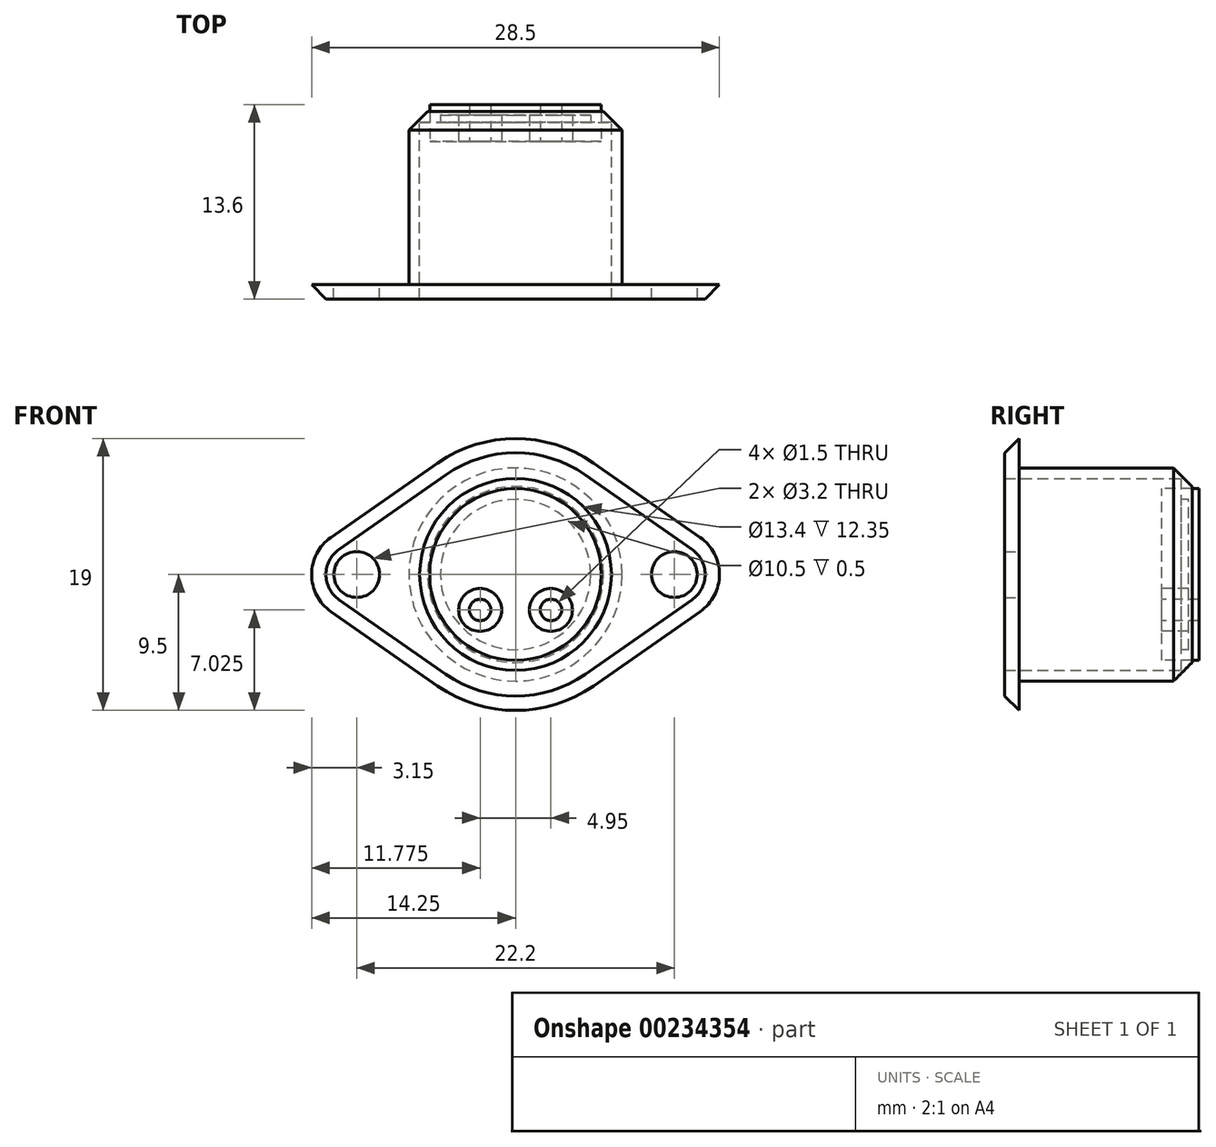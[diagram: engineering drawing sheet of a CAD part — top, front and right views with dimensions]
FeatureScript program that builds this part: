
annotation { "Feature Type Name" : "Feature", "Feature Type Description" : "" }
export const myFeature = defineFeature(function(context is Context, id is Id, definition is map)
    precondition{}
    {
        {
            var Q0;
            Q0=qCreatedBy(makeId("Front.planeOp"),FACE);
            var sketch = newSketch(context, id + "F0", { "sketchPlane" : qUnion([Q0])});
            skCircle(sketch, "E0", {"center": v(-11.1, 0) * mm, "radius": 1.6 * mm});
            skCircle(sketch, "E1", {"center": v(11.1, 0) * mm, "radius": 1.6 * mm});
            skArc(sketch, "E2", {"start": v(-12.9, 2.58) * mm, "mid": v(-14.25, 0) * mm, "end": v(-12.9, -2.58) * mm});
            skLineSegment(sketch, "E3", {"start": v(-14.25, 0) * mm, "end": v(14.25, 0) * mm, "construction": true});
            skCircle(sketch, "E4", {"center": v(0, 0) * mm, "radius": 6 * mm});
            skCircle(sketch, "E5", {"center": v(0, 0) * mm, "radius": 6.7 * mm});
            skArc(sketch, "E6", {"start": v(5.43, 7.8) * mm, "mid": v(0, 9.5) * mm, "end": v(-5.43, 7.8) * mm});
            skLineSegment(sketch, "E7", {"start": v(-12.9, 2.58) * mm, "end": v(-5.43, 7.8) * mm});
            skLineSegment(sketch, "E8", {"start": v(-12.9, -2.58) * mm, "end": v(-5.43, -7.8) * mm});
            skArc(sketch, "E9", {"start": v(12.9, -2.58) * mm, "mid": v(14.25, 0) * mm, "end": v(12.9, 2.58) * mm});
            skLineSegment(sketch, "E10", {"start": v(5.43, 7.8) * mm, "end": v(12.9, 2.58) * mm});
            skLineSegment(sketch, "E11", {"start": v(5.43, -7.8) * mm, "end": v(12.9, -2.58) * mm});
            skArc(sketch, "E12.trimOffspring", {"start": v(-5.43, -7.8) * mm, "mid": v(0, -9.5) * mm, "end": v(5.43, -7.8) * mm});
            skCircle(sketch, "E13.1.0", {"center": v(-2.47, 2.47) * mm, "radius": 0.75 * mm});
            skCircle(sketch, "E13.3.0", {"center": v(2.47, 2.47) * mm, "radius": 0.75 * mm});
            skLineSegment(sketch, "E13.anchor1", {"start": v(0, 0) * mm, "end": v(-3.5, 0) * mm, "construction": true});
            skLineSegment(sketch, "E13.anchor2", {"start": v(0, 0) * mm, "end": v(3.5, 0) * mm, "construction": true});
            skCircle(sketch, "E14", {"center": v(0, 0) * mm, "radius": 7.45 * mm});
            skLineSegment(sketch, "E15", {"start": v(0, 0) * mm, "end": v(2.47, 2.47) * mm, "construction": true});
            skLineSegment(sketch, "E16", {"start": v(0, 0) * mm, "end": v(-2.47, 2.47) * mm, "construction": true});
            skLineSegment(sketch, "E17.MirrorCS", {"start": v(0, 0) * mm, "end": v(-2.47, -2.47) * mm, "construction": true});
            skCircle(sketch, "E18.MirrorC", {"center": v(-2.47, -2.47) * mm, "radius": 0.75 * mm});
            skCircle(sketch, "E19.MirrorC", {"center": v(2.47, -2.47) * mm, "radius": 0.75 * mm});
            skLineSegment(sketch, "E20.left", {"start": v(-3.92, -1) * mm, "end": v(-3.92, 1) * mm});
            skLineSegment(sketch, "E21", {"start": v(0, -2.47) * mm, "end": v(0, 2.47) * mm, "construction": true});
            skLineSegment(sketch, "E22.MirrorCS", {"start": v(3.92, -1) * mm, "end": v(3.92, 1) * mm});
            skLineSegment(sketch, "E23", {"start": v(-3.92, 1) * mm, "end": v(-5.92, 1) * mm});
            skLineSegment(sketch, "E24", {"start": v(-3.92, -1) * mm, "end": v(-5.92, -1) * mm});
            skLineSegment(sketch, "E25.MirrorCS", {"start": v(3.92, 1) * mm, "end": v(5.92, 1) * mm});
            skLineSegment(sketch, "E26.MirrorCS", {"start": v(3.92, -1) * mm, "end": v(5.92, -1) * mm});
            skCircle(sketch, "E27", {"center": v(0, 0) * mm, "radius": 0.75 * mm});
            skSolve(sketch);
        }
        {
            var Q0;
            Q0=makeQuery(id+"F0.imprint","IMPRINT",FACE,{"disambiguationData":[TD([[makeQuery(id+"F0.imprint","IMPRINT",EDGE,{"derivedFrom":sQuery(id+"F0.wireOp",EDGE,"E0")}),-1.0]])]});
            var Q1;
            Q1=makeQuery(id+"F0.imprint","IMPRINT",FACE,{"disambiguationData":[TD([[makeQuery(id+"F0.imprint","IMPRINT",EDGE,{"derivedFrom":sQuery(id+"F0.wireOp",EDGE,"E5")}),-1.0]])]});
            extrude(context, id + "F1", {"entities" : qUnion([Q0, Q1]), "depth" : 1 * mm});
        }
        {
            var Q0;
            Q0=makeQuery(id+"F1.opExtrude","CAP_EDGE",EDGE,{"disambiguationData":[OSD([sQuery(id+"F0.wireOp",EDGE,"E7")])],"isStart":false});
            chamfer(context, id + "F2", {"entities" : qUnion([Q0]), "width" : 1 * mm, "tangentPropagation" : true});
        }
        {
            var Q0;
            Q0=makeQuery(id+"F0.imprint","IMPRINT",FACE,{"disambiguationData":[TD([[makeQuery(id+"F0.imprint","IMPRINT",EDGE,{"derivedFrom":sQuery(id+"F0.wireOp",EDGE,"E5")}),-1.0]])]});
            var Q1;
            Q1=makeQuery(id+"F0.imprint","IMPRINT",FACE,{"disambiguationData":[TD([[makeQuery(id+"F0.imprint","IMPRINT",EDGE,{"derivedFrom":sQuery(id+"F0.wireOp",EDGE,"E4")}),-1.0]])]});
            var Q2;
            Q2=makeQuery(id+"F0.imprint","IMPRINT",FACE,{"disambiguationData":[TD([[makeQuery(id+"F0.imprint","IMPRINT",EDGE,{"derivedFrom":sQuery(id+"F0.wireOp",EDGE,"E4")}),1.0]])]});
            var Q3;
            Q3=makeQuery(id+"F0.imprint","IMPRINT",FACE,{"disambiguationData":[TD([[makeQuery(id+"F0.imprint","IMPRINT",EDGE,{"derivedFrom":sQuery(id+"F0.wireOp",EDGE,"E18.MirrorC")}),-1.0]])]});
            var Q4;
            Q4=makeQuery(id+"F0.imprint","IMPRINT",FACE,{"disambiguationData":[TD([[makeQuery(id+"F0.imprint","IMPRINT",EDGE,{"derivedFrom":sQuery(id+"F0.wireOp",EDGE,"E19.MirrorC")}),-1.0]])]});
            var Q5;
            Q5=makeQuery(id+"F0.imprint","IMPRINT",FACE,{"disambiguationData":[TD([[makeQuery(id+"F0.imprint","IMPRINT",EDGE,{"derivedFrom":sQuery(id+"F0.wireOp",EDGE,"E13.1.0")}),1.0]])]});
            var Q6;
            Q6=makeQuery(id+"F0.imprint","IMPRINT",FACE,{"disambiguationData":[TD([[makeQuery(id+"F0.imprint","IMPRINT",EDGE,{"derivedFrom":sQuery(id+"F0.wireOp",EDGE,"E13.3.0")}),1.0]])]});
            var Q7;
            Q7=makeQuery(id+"F0.imprint","IMPRINT",FACE,{"disambiguationData":[TD([[makeQuery(id+"F0.imprint","IMPRINT",EDGE,{"derivedFrom":sQuery(id+"F0.wireOp",EDGE,"E20.left")}),1.0]])]});
            var Q8;
            Q8=makeQuery(id+"F0.imprint","IMPRINT",FACE,{"disambiguationData":[TD([[makeQuery(id+"F0.imprint","IMPRINT",EDGE,{"derivedFrom":sQuery(id+"F0.wireOp",EDGE,"E22.MirrorCS")}),-1.0]])]});
            var Q9;
            Q9=makeQuery(id+"F0.imprint","IMPRINT",FACE,{"disambiguationData":[TD([[makeQuery(id+"F0.imprint","IMPRINT",EDGE,{"derivedFrom":sQuery(id+"F0.wireOp",EDGE,"E27")}),1.0]])]});
            var Q10;
            Q10=sQuery(id+"F0.wireOp",EDGE,"E5");
            extrude(context, id + "F3", {"entities" : qUnion([Q0, Q1, Q2, Q3, Q4, Q5, Q6, Q7, Q8, Q9]), "operationType" : NewBodyOperationType.ADD, "surfaceEntities" : qUnion([Q10]), "oppositeDirection" : true, "depth" : 12.1 * mm});
        }
        {
            var Q0;
            Q0=makeQuery(id+"F3.opExtrude","CAP_FACE",FACE,{"disambiguationData":[OSD([sQuery(id+"F0.wireOp",EDGE,"E14")])],"isStart":true});
            shell(context, id + "F4", {"entities" : qUnion([Q0]), "thickness" : .75 * mm});
        }
        {
            var Q0;
            Q0=makeQuery(id+"F0.imprint","IMPRINT",FACE,{"disambiguationData":[TD([[makeQuery(id+"F0.imprint","IMPRINT",EDGE,{"derivedFrom":sQuery(id+"F0.wireOp",EDGE,"TtFvNPpV-GBaN-JR9W-IqtY-BeMt7pxMo1nd")}),-1.0]])]});
            var Q1;
            Q1=makeQuery(id+"F0.imprint","IMPRINT",FACE,{"disambiguationData":[TD([[makeQuery(id+"F0.imprint","IMPRINT",EDGE,{"derivedFrom":sQuery(id+"F0.wireOp",EDGE,"TtFvNPpV-GBaN-JR9W-IqtY-BeMt7pxMo1nd")}),1.0]])]});
            var Q2;
            Q2=makeQuery(id+"F0.imprint","IMPRINT",FACE,{"disambiguationData":[TD([[makeQuery(id+"F0.imprint","IMPRINT",EDGE,{"derivedFrom":sQuery(id+"F0.wireOp",EDGE,"E13.1.0")}),1.0]])]});
            var Q3;
            Q3=makeQuery(id+"F0.imprint","IMPRINT",FACE,{"disambiguationData":[TD([[makeQuery(id+"F0.imprint","IMPRINT",EDGE,{"derivedFrom":sQuery(id+"F0.wireOp",EDGE,"E13.2.0")}),1.0]])]});
            var Q4;
            Q4=makeQuery(id+"F0.imprint","IMPRINT",FACE,{"disambiguationData":[TD([[makeQuery(id+"F0.imprint","IMPRINT",EDGE,{"derivedFrom":sQuery(id+"F0.wireOp",EDGE,"E13.3.0")}),1.0]])]});
            var Q5;
            Q5=makeQuery(id+"F0.imprint","IMPRINT",FACE,{"disambiguationData":[TD([[makeQuery(id+"F0.imprint","IMPRINT",EDGE,{"derivedFrom":sQuery(id+"F0.wireOp",EDGE,"E13.4.0")}),1.0]])]});
            var Q6;
            {var subQ0=sQuery(id+"F0.wireOp",EDGE,"y8nhEUVQ-kyqU-Q8um-lzXM-BuWz2Y8k01lN");Q6=makeQuery(id+"F0.imprint","IMPRINT",FACE,{"disambiguationData":[TD([[makeQuery(id+"F0.imprint","IMPRINT",EDGE,{"derivedFrom":subQ0}),-1.0]])]});}
            var Q7;
            Q7=makeQuery(id+"F0.imprint","IMPRINT",FACE,{"disambiguationData":[TD([[makeQuery(id+"F0.imprint","IMPRINT",EDGE,{"derivedFrom":sQuery(id+"F0.wireOp",EDGE,"E18.MirrorC")}),-1.0]])]});
            var Q8;
            Q8=makeQuery(id+"F0.imprint","IMPRINT",FACE,{"disambiguationData":[TD([[makeQuery(id+"F0.imprint","IMPRINT",EDGE,{"derivedFrom":sQuery(id+"F0.wireOp",EDGE,"E19.MirrorC")}),-1.0]])]});
            var Q9;
            Q9=makeQuery(id+"F0.imprint","IMPRINT",FACE,{"disambiguationData":[TD([[makeQuery(id+"F0.imprint","IMPRINT",EDGE,{"derivedFrom":sQuery(id+"F0.wireOp",EDGE,"E4")}),1.0]])]});
            var Q10;
            Q10=makeQuery(id+"F0.imprint","IMPRINT",FACE,{"disambiguationData":[TD([[makeQuery(id+"F0.imprint","IMPRINT",EDGE,{"derivedFrom":sQuery(id+"F0.wireOp",EDGE,"E20.left")}),1.0]])]});
            var Q11;
            Q11=makeQuery(id+"F0.imprint","IMPRINT",FACE,{"disambiguationData":[TD([[makeQuery(id+"F0.imprint","IMPRINT",EDGE,{"derivedFrom":sQuery(id+"F0.wireOp",EDGE,"E22.MirrorCS")}),-1.0]])]});
            var Q12;
            Q12=makeQuery(id+"F0.imprint","IMPRINT",FACE,{"disambiguationData":[TD([[makeQuery(id+"F0.imprint","IMPRINT",EDGE,{"derivedFrom":sQuery(id+"F0.wireOp",EDGE,"E27")}),1.0]])]});
            extrude(context, id + "F5", {"entities" : qUnion([Q0, Q1, Q2, Q3, Q4, Q5, Q6, Q7, Q8, Q9, Q10, Q11, Q12]), "oppositeDirection" : true, "depth" : 12.6 * mm});
        }
        {
            var Q0;
            Q0=makeQuery(id+"F0.imprint","IMPRINT",FACE,{"disambiguationData":[TD([[makeQuery(id+"F0.imprint","IMPRINT",EDGE,{"derivedFrom":sQuery(id+"F0.wireOp",EDGE,"E18.MirrorC")}),-1.0]])]});
            var Q1;
            Q1=makeQuery(id+"F0.imprint","IMPRINT",FACE,{"disambiguationData":[TD([[makeQuery(id+"F0.imprint","IMPRINT",EDGE,{"derivedFrom":sQuery(id+"F0.wireOp",EDGE,"E13.1.0")}),1.0]])]});
            var Q2;
            Q2=makeQuery(id+"F0.imprint","IMPRINT",FACE,{"disambiguationData":[TD([[makeQuery(id+"F0.imprint","IMPRINT",EDGE,{"derivedFrom":sQuery(id+"F0.wireOp",EDGE,"E13.3.0")}),1.0]])]});
            var Q3;
            Q3=makeQuery(id+"F0.imprint","IMPRINT",FACE,{"disambiguationData":[TD([[makeQuery(id+"F0.imprint","IMPRINT",EDGE,{"derivedFrom":sQuery(id+"F0.wireOp",EDGE,"E19.MirrorC")}),-1.0]])]});
            var Q4;
            Q4=makeQuery(id+"F0.imprint","IMPRINT",FACE,{"disambiguationData":[TD([[makeQuery(id+"F0.imprint","IMPRINT",EDGE,{"derivedFrom":sQuery(id+"F0.wireOp",EDGE,"E27")}),1.0]])]});
            var Q5;
            Q5=makeQuery(id+"F0.imprint","IMPRINT",FACE,{"disambiguationData":[TD([[makeQuery(id+"F0.imprint","IMPRINT",EDGE,{"derivedFrom":sQuery(id+"F0.wireOp",EDGE,"E20.left")}),1.0]])]});
            var Q6;
            Q6=makeQuery(id+"F0.imprint","IMPRINT",FACE,{"disambiguationData":[TD([[makeQuery(id+"F0.imprint","IMPRINT",EDGE,{"derivedFrom":sQuery(id+"F0.wireOp",EDGE,"E22.MirrorCS")}),-1.0]])]});
            extrude(context, id + "F6", {"entities" : qUnion([Q0, Q1, Q2, Q3, Q4, Q5, Q6]), "operationType" : NewBodyOperationType.REMOVE, "oppositeDirection" : true, "depth" : 10 * mm});
        }
        {
            var Q0;
            Q0=makeQuery(id+"F3.opExtrude","CAP_EDGE",EDGE,{"disambiguationData":[OSD([sQuery(id+"F0.wireOp",EDGE,"E14")])],"isStart":false});
            chamfer(context, id + "F7", {"entities" : qUnion([Q0]), "width" : 1.3 * mm, "tangentPropagation" : true});
        }
    });
